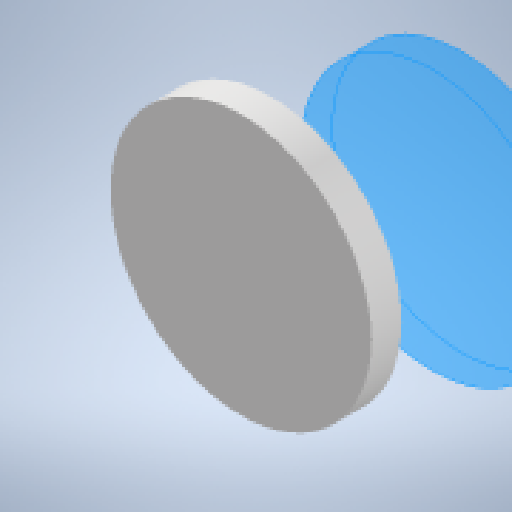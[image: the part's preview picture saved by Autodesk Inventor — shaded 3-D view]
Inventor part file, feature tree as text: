
AUTODESK INVENTOR PART (.ipt)
format: ipt  version: 2024 (Build 280153000, 153)  size: 125,440 bytes
history: native  units: in
note: dims shown in document units (in); Inventor stores cm internally (conversion verified against a paired STEP export)
features: extrude x1, sketch x1
ambient origin geometry x8: Origin, YZ Plane, XZ Plane, XY Plane, X Axis, Y Axis, Z Axis, Center Point
bodies: Solid1 (feature_tree)
feature tree (2):
  extrude  "Extrusion1"  [1 undecoded]
  sketch  "Sketch1"  dims[d0=0.2in d1=0.0in]
note: 1 required parameter value undecoded (feature->parameter linkage not recoverable at this tier; creation-order binding heuristic only, values carry confidence <= 0.55)
